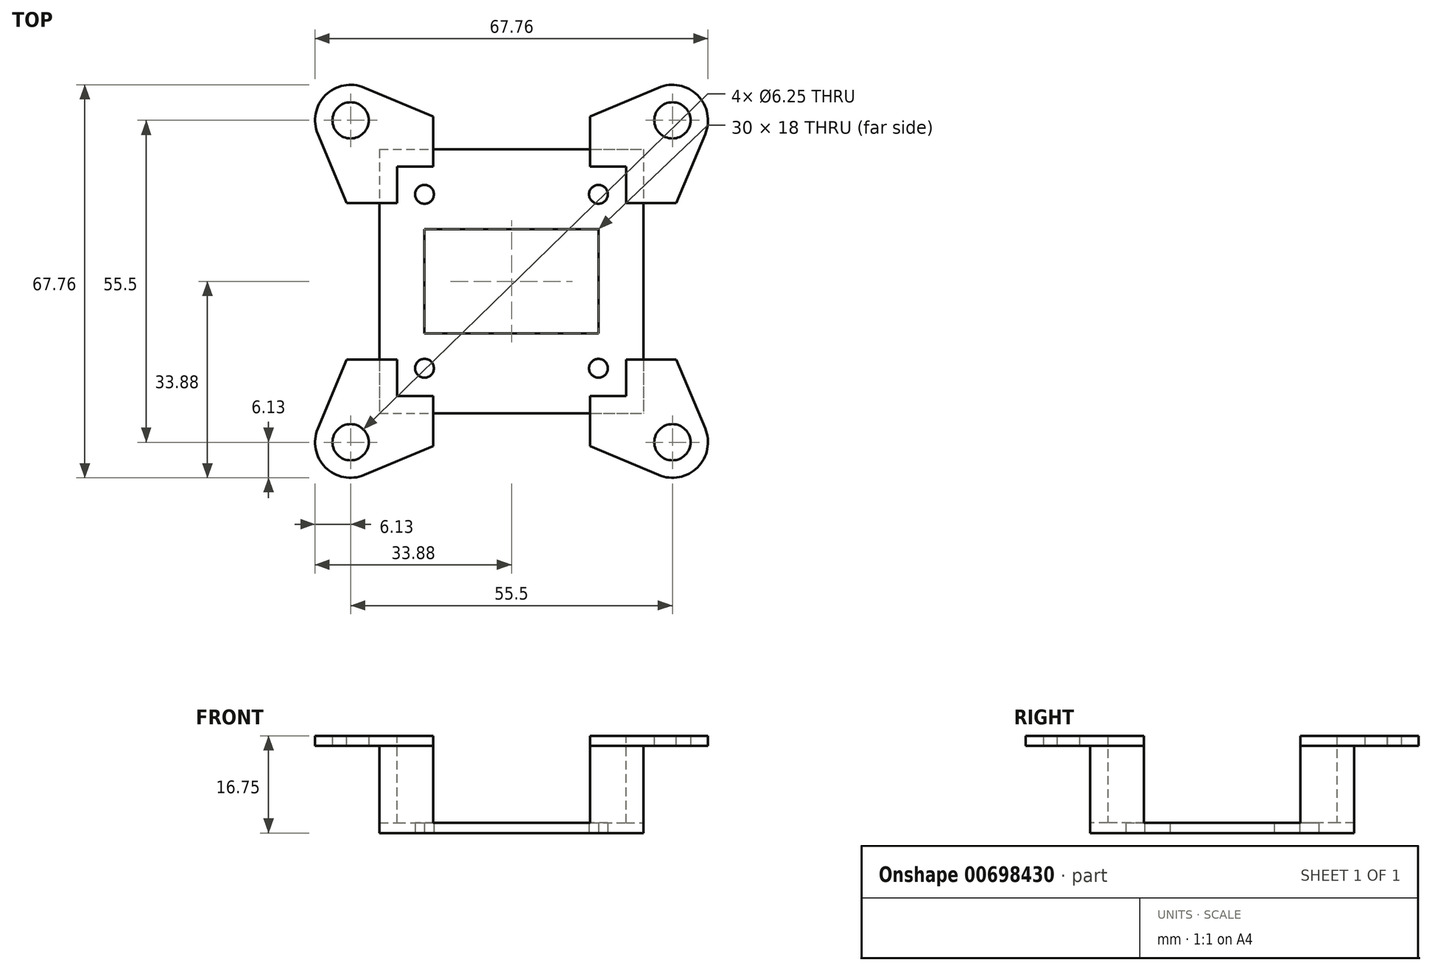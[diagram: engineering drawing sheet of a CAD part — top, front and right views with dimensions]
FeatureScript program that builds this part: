
annotation { "Feature Type Name" : "Feature", "Feature Type Description" : "" }
export const myFeature = defineFeature(function(context is Context, id is Id, definition is map)
    precondition{}
    {
        {
            var Q0;
            Q0=qCreatedBy(makeId("Top.planeOp"),FACE);
            var sketch = newSketch(context, id + "F0", { "sketchPlane" : qUnion([Q0])});
            skCircle(sketch, "E0", {"center": v(-15, 15) * mm, "radius": 1.63 * mm});
            skCircle(sketch, "E1", {"center": v(15, 15) * mm, "radius": 1.63 * mm});
            skCircle(sketch, "E2", {"center": v(15, -15) * mm, "radius": 1.63 * mm});
            skCircle(sketch, "E3", {"center": v(-15, -15) * mm, "radius": 1.63 * mm});
            skLineSegment(sketch, "E4.bottom", {"start": v(-15, 9) * mm, "end": v(15, 9) * mm});
            skLineSegment(sketch, "E4.top", {"start": v(-15, -9) * mm, "end": v(15, -9) * mm});
            skLineSegment(sketch, "E4.left", {"start": v(-15, 9) * mm, "end": v(-15, -9) * mm});
            skLineSegment(sketch, "E4.right", {"start": v(15, 9) * mm, "end": v(15, -9) * mm});
            skLineSegment(sketch, "E5.bottom", {"start": v(-19.75, 19.75) * mm, "end": v(19.75, 19.75) * mm});
            skLineSegment(sketch, "E5.top", {"start": v(-19.75, -19.75) * mm, "end": v(19.75, -19.75) * mm});
            skLineSegment(sketch, "E5.left", {"start": v(-19.75, 19.75) * mm, "end": v(-19.75, -19.75) * mm});
            skLineSegment(sketch, "E5.right", {"start": v(19.75, 19.75) * mm, "end": v(19.75, -19.75) * mm});
            skSolve(sketch);
        }
        {
            var Q0;
            Q0=makeQuery(id+"F0.imprint","IMPRINT",FACE,{"disambiguationData":[TD([[makeQuery(id+"F0.imprint","IMPRINT",EDGE,{"derivedFrom":sQuery(id+"F0.wireOp",EDGE,"E0")}),-1.0]])]});
            extrude(context, id + "F1", {"entities" : qUnion([Q0]), "depth" : 1.75 * mm, "offsetDistance" : 25 * mm});
        }
        {
            var Q0;
            Q0=qCreatedBy(makeId("Top.planeOp"),FACE);
            var sketch = newSketch(context, id + "F2", { "sketchPlane" : qUnion([Q0])});
            skLineSegment(sketch, "E6.bottom", {"start": v(-22.75, 22.75) * mm, "end": v(22.75, 22.75) * mm});
            skLineSegment(sketch, "E6.top", {"start": v(-22.75, -22.75) * mm, "end": v(22.75, -22.75) * mm});
            skLineSegment(sketch, "E6.left", {"start": v(-22.75, 22.75) * mm, "end": v(-22.75, -22.75) * mm});
            skLineSegment(sketch, "E6.right", {"start": v(22.75, 22.75) * mm, "end": v(22.75, -22.75) * mm});
            skLineSegment(sketch, "E7.bottom", {"start": v(-19.75, 19.75) * mm, "end": v(19.75, 19.75) * mm});
            skLineSegment(sketch, "E7.top", {"start": v(-19.75, -19.75) * mm, "end": v(19.75, -19.75) * mm});
            skLineSegment(sketch, "E7.left", {"start": v(-19.75, 19.75) * mm, "end": v(-19.75, -19.75) * mm});
            skLineSegment(sketch, "E7.right", {"start": v(19.75, 19.75) * mm, "end": v(19.75, -19.75) * mm});
            skSolve(sketch);
        }
        {
            var Q0;
            Q0 = qSketchRegion(id + "F2", true);
            extrude(context, id + "F3", {"entities" : qUnion([Q0]), "operationType" : NewBodyOperationType.ADD, "depth" : 15 * mm, "offsetDistance" : 25 * mm});
        }
        {
            var Q0;
            Q0=makeQuery(id+"F3.opExtrude","CAP_FACE",FACE,{"disambiguationData":[OSD([sQuery(id+"F2.wireOp",EDGE,"E6.bottom"),sQuery(id+"F2.wireOp",EDGE,"E6.top"),sQuery(id+"F2.wireOp",EDGE,"E6.left"),sQuery(id+"F2.wireOp",EDGE,"E6.right"),sQuery(id+"F2.wireOp",EDGE,"E7.bottom"),sQuery(id+"F2.wireOp",EDGE,"E7.top"),sQuery(id+"F2.wireOp",EDGE,"E7.left"),sQuery(id+"F2.wireOp",EDGE,"E7.right")])],"isStart":false});
            var sketch = newSketch(context, id + "F4", { "sketchPlane" : qUnion([Q0])});
            skCircle(sketch, "E8", {"center": v(-27.75, 27.75) * mm, "radius": 3.12 * mm});
            skCircle(sketch, "E9", {"center": v(27.75, 27.75) * mm, "radius": 3.12 * mm});
            skCircle(sketch, "E10", {"center": v(27.75, -27.75) * mm, "radius": 3.12 * mm});
            skCircle(sketch, "E11", {"center": v(-27.75, -27.75) * mm, "radius": 3.12 * mm});
            skArc(sketch, "E12", {"start": v(-25.38, 33.4) * mm, "mid": v(-32.08, 32.08) * mm, "end": v(-33.4, 25.38) * mm});
            skArc(sketch, "E13", {"start": v(33.4, 25.38) * mm, "mid": v(32.08, 32.08) * mm, "end": v(25.38, 33.4) * mm});
            skArc(sketch, "E14", {"start": v(25.38, -33.4) * mm, "mid": v(32.08, -32.08) * mm, "end": v(33.4, -25.38) * mm});
            skArc(sketch, "E15", {"start": v(-33.4, -25.38) * mm, "mid": v(-32.08, -32.08) * mm, "end": v(-25.38, -33.4) * mm});
            skLineSegment(sketch, "E16", {"start": v(-33.4, 25.38) * mm, "end": v(-22.75, 0) * mm});
            skLineSegment(sketch, "E17", {"start": v(-22.75, 0) * mm, "end": v(-33.4, -25.38) * mm});
            skLineSegment(sketch, "E18", {"start": v(-25.38, -33.4) * mm, "end": v(0, -22.75) * mm});
            skLineSegment(sketch, "E19", {"start": v(0, -22.75) * mm, "end": v(25.38, -33.4) * mm});
            skLineSegment(sketch, "E20", {"start": v(33.4, -25.38) * mm, "end": v(22.75, 0) * mm});
            skLineSegment(sketch, "E21", {"start": v(22.75, 0) * mm, "end": v(33.4, 25.38) * mm});
            skLineSegment(sketch, "E22", {"start": v(-25.38, 33.4) * mm, "end": v(0, 22.75) * mm});
            skLineSegment(sketch, "E23", {"start": v(0, 22.75) * mm, "end": v(25.38, 33.4) * mm});
            skLineSegment(sketch, "E24.bottom", {"start": v(-19.75, 19.75) * mm, "end": v(19.75, 19.75) * mm});
            skLineSegment(sketch, "E24.top", {"start": v(-19.75, -19.75) * mm, "end": v(19.75, -19.75) * mm});
            skLineSegment(sketch, "E24.left", {"start": v(-19.75, 19.75) * mm, "end": v(-19.75, -19.75) * mm});
            skLineSegment(sketch, "E24.right", {"start": v(19.75, 19.75) * mm, "end": v(19.75, -19.75) * mm});
            skSolve(sketch);
        }
        {
            var Q0;
            Q0 = qSketchRegion(id + "F4", true);
            extrude(context, id + "F5", {"entities" : qUnion([Q0]), "operationType" : NewBodyOperationType.ADD, "depth" : 1.75 * mm, "offsetDistance" : 25 * mm});
        }
        {
            var Q0;
            Q0=makeQuery(id+"F3.opExtrude","SWEPT_FACE",FACE,{"disambiguationData":[OSD([sQuery(id+"F2.wireOp",EDGE,"E6.top")])]});
            var sketch = newSketch(context, id + "F6", { "sketchPlane" : qUnion([Q0])});
            skLineSegment(sketch, "E25.bottom", {"start": v(-13.5, 1.75) * mm, "end": v(13.55, 1.75) * mm});
            skLineSegment(sketch, "E25.top", {"start": v(-13.5, 16.75) * mm, "end": v(13.55, 16.75) * mm});
            skLineSegment(sketch, "E25.left", {"start": v(-13.5, 1.75) * mm, "end": v(-13.5, 16.75) * mm});
            skLineSegment(sketch, "E25.right", {"start": v(13.55, 1.75) * mm, "end": v(13.55, 16.75) * mm});
            skSolve(sketch);
        }
        {
            var Q0;
            Q0 = qSketchRegion(id + "F6", true);
            extrude(context, id + "F7", {"entities" : qUnion([Q0]), "operationType" : NewBodyOperationType.REMOVE, "depth" : 25 * mm, "offsetDistance" : 25 * mm});
        }
        {
            var Q0;
            Q0 = qSketchRegion(id + "F6", true);
            extrude(context, id + "F8", {"entities" : qUnion([Q0]), "operationType" : NewBodyOperationType.REMOVE, "endBound" : BoundingType.THROUGH_ALL, "oppositeDirection" : true, "depth" : 22 * mm, "offsetDistance" : 25 * mm});
        }
        {
            var Q0;
            Q0=makeQuery(id+"F3.opExtrude","SWEPT_FACE",FACE,{"disambiguationData":[OSD([sQuery(id+"F2.wireOp",EDGE,"E6.right")])]});
            var sketch = newSketch(context, id + "F9", { "sketchPlane" : qUnion([Q0])});
            skLineSegment(sketch, "E26.bottom", {"start": v(-13.5, 1.75) * mm, "end": v(13.5, 1.75) * mm});
            skLineSegment(sketch, "E26.top", {"start": v(-13.5, 16.75) * mm, "end": v(13.5, 16.75) * mm});
            skLineSegment(sketch, "E26.left", {"start": v(-13.5, 1.75) * mm, "end": v(-13.5, 16.75) * mm});
            skLineSegment(sketch, "E26.right", {"start": v(13.5, 1.75) * mm, "end": v(13.5, 16.75) * mm});
            skSolve(sketch);
        }
        {
            var Q0;
            Q0 = qSketchRegion(id + "F9", true);
            extrude(context, id + "F10", {"entities" : qUnion([Q0]), "operationType" : NewBodyOperationType.REMOVE, "endBound" : BoundingType.THROUGH_ALL, "depth" : 25 * mm, "offsetDistance" : 25 * mm});
        }
        {
            var Q0;
            Q0 = qSketchRegion(id + "F9", true);
            extrude(context, id + "F11", {"entities" : qUnion([Q0]), "operationType" : NewBodyOperationType.REMOVE, "endBound" : BoundingType.THROUGH_ALL, "oppositeDirection" : true, "depth" : 25 * mm, "offsetDistance" : 25 * mm});
        }
    });
